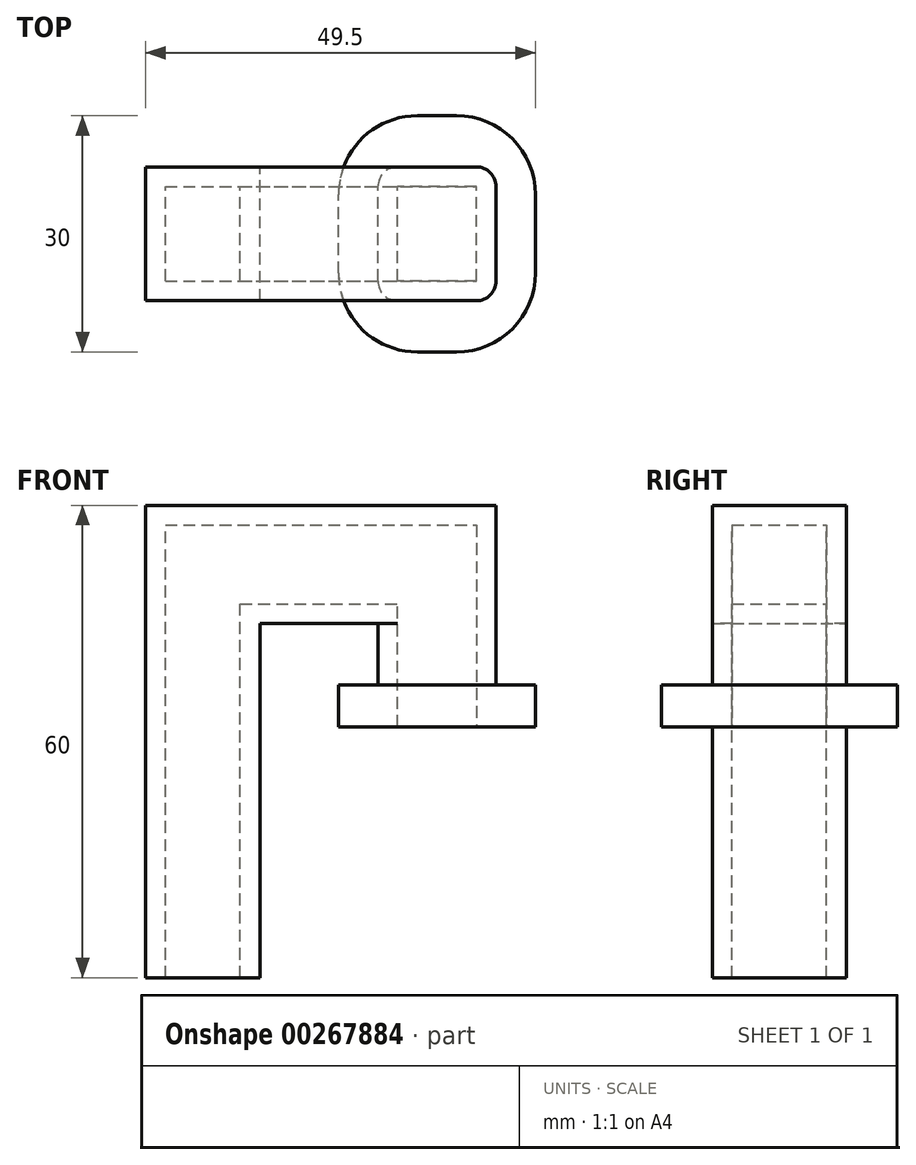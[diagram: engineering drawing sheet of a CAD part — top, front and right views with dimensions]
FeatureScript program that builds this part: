
annotation { "Feature Type Name" : "Feature", "Feature Type Description" : "" }
export const myFeature = defineFeature(function(context is Context, id is Id, definition is map)
    precondition{}
    {
        {
            var Q0;
            Q0=qCreatedBy(makeId("Front.planeOp"),FACE);
            var sketch = newSketch(context, id + "F0", { "sketchPlane" : qUnion([Q0])});
            skLineSegment(sketch, "E0", {"start": v(-4.8, -0.41) * mm, "end": v(-4.8, 59.59) * mm});
            skLineSegment(sketch, "E1", {"start": v(-4.8, -0.41) * mm, "end": v(9.7, -0.41) * mm});
            skLineSegment(sketch, "E2", {"start": v(9.7, -0.41) * mm, "end": v(9.7, 44.59) * mm});
            skLineSegment(sketch, "E3", {"start": v(9.7, 44.59) * mm, "end": v(24.7, 44.59) * mm});
            skLineSegment(sketch, "E4", {"start": v(39.7, 59.59) * mm, "end": v(39.7, 36.77) * mm});
            skLineSegment(sketch, "E5", {"start": v(39.7, 36.77) * mm, "end": v(24.7, 36.77) * mm});
            skLineSegment(sketch, "E6", {"start": v(24.7, 36.77) * mm, "end": v(24.7, 44.59) * mm});
            skLineSegment(sketch, "E7", {"start": v(24.7, 36.77) * mm, "end": v(19.7, 36.77) * mm});
            skLineSegment(sketch, "E8", {"start": v(19.7, 36.77) * mm, "end": v(19.7, 31.46) * mm});
            skLineSegment(sketch, "E9", {"start": v(19.7, 31.46) * mm, "end": v(44.7, 31.46) * mm});
            skLineSegment(sketch, "E10", {"start": v(44.7, 31.46) * mm, "end": v(44.7, 36.77) * mm});
            skLineSegment(sketch, "E11", {"start": v(44.7, 36.77) * mm, "end": v(39.7, 36.77) * mm});
            skLineSegment(sketch, "E12", {"start": v(-4.8, 59.59) * mm, "end": v(39.7, 59.59) * mm});
            skSolve(sketch);
        }
        {
            var Q0;
            Q0=makeQuery(id+"F0.imprint","IMPRINT",FACE,{"disambiguationData":[TD([[makeQuery(id+"F0.imprint","IMPRINT",EDGE,{"derivedFrom":sQuery(id+"F0.wireOp",EDGE,"E0")}),-1.0]])]});
            extrude(context, id + "F1", {"entities" : qUnion([Q0]), "endBound" : BoundingType.SYMMETRIC, "depth" : 17 * mm});
        }
        {
            var Q0;
            Q0=makeQuery(id+"F1.opExtrude","SWEPT_FACE",FACE,{"disambiguationData":[OSD([sQuery(id+"F0.wireOp",EDGE,"E1")])]});
            shell(context, id + "F2", {"entities" : qUnion([Q0]), "thickness" : 2.5 * mm});
        }
        {
            var Q0;
            Q0=makeQuery(id+"F0.imprint","IMPRINT",FACE,{"disambiguationData":[TD([[makeQuery(id+"F0.imprint","IMPRINT",EDGE,{"derivedFrom":sQuery(id+"F0.wireOp",EDGE,"E5")}),1.0]])]});
            extrude(context, id + "F3", {"entities" : qUnion([Q0]), "operationType" : NewBodyOperationType.ADD, "endBound" : BoundingType.SYMMETRIC, "depth" : 30 * mm});
        }
        {
            var Q0;
            Q0=makeQuery(id+"F3.opExtrude","SWEPT_FACE",FACE,{"disambiguationData":[OSD([sQuery(id+"F0.wireOp",EDGE,"E9")])]});
            var sketch = newSketch(context, id + "F4", { "sketchPlane" : qUnion([Q0])});
            skPoint(sketch, "E13.0", {"position": v(32.2, 15) * mm});
            skPoint(sketch, "E14.0", {"position": v(44.7, 0) * mm});
            skPoint(sketch, "E15.middle", {"position": v(32.2, 0) * mm});
            skLineSegment(sketch, "E16.0.0", {"start": v(44.7, -15) * mm, "end": v(19.7, -15) * mm});
            skLineSegment(sketch, "E16.0.1", {"start": v(19.7, -15) * mm, "end": v(19.7, 15) * mm});
            skLineSegment(sketch, "E16.0.2", {"start": v(19.7, 15) * mm, "end": v(44.7, 15) * mm});
            skLineSegment(sketch, "E16.0.3", {"start": v(44.7, 15) * mm, "end": v(44.7, -15) * mm});
            skLineSegment(sketch, "E17.0", {"start": v(39.7, 8.5) * mm, "end": v(39.7, -8.5) * mm});
            skLineSegment(sketch, "E18.0", {"start": v(39.7, 8.5) * mm, "end": v(24.7, 8.5) * mm});
            skLineSegment(sketch, "E19.0", {"start": v(24.7, 8.5) * mm, "end": v(24.7, -8.5) * mm});
            skLineSegment(sketch, "E20.0", {"start": v(39.7, -8.5) * mm, "end": v(24.7, -8.5) * mm});
            skLineSegment(sketch, "E21.0", {"start": v(37.2, 6) * mm, "end": v(37.2, -6) * mm});
            skLineSegment(sketch, "E22.0", {"start": v(37.2, -6) * mm, "end": v(27.2, -6) * mm});
            skLineSegment(sketch, "E23.0", {"start": v(37.2, 6) * mm, "end": v(27.2, 6) * mm});
            skLineSegment(sketch, "E24.0", {"start": v(27.2, 6) * mm, "end": v(27.2, -6) * mm});
            skSolve(sketch);
        }
        {
            var Q0;
            Q0=makeQuery(id+"F4.imprint","IMPRINT",FACE,{"disambiguationData":[TD([[makeQuery(id+"F4.imprint","IMPRINT",EDGE,{"derivedFrom":sQuery(id+"F4.wireOp",EDGE,"E21.0")}),-1.0]])]});
            var Q1;
            Q1=makeQuery(id+"F3.opExtrude","SWEPT_FACE",FACE,{"disambiguationData":[OSD([sQuery(id+"F0.wireOp",EDGE,"E5"),sQuery(id+"F0.wireOp",EDGE,"E7"),sQuery(id+"F0.wireOp",EDGE,"E11")])]});
            extrude(context, id + "F5", {"entities" : qUnion([Q0]), "operationType" : NewBodyOperationType.REMOVE, "oppositeDirection" : true, "endBoundEntityFace" : qUnion([Q1]), "depth" : 10 * mm});
        }
        {
            var Q0;
            Q0=makeQuery(id+"F3.opExtrude","CAP_EDGE",EDGE,{"disambiguationData":[OSD([sQuery(id+"F0.wireOp",EDGE,"E10")])],"isStart":false});
            var Q1;
            Q1=makeQuery(id+"F3.opExtrude","CAP_EDGE",EDGE,{"disambiguationData":[OSD([sQuery(id+"F0.wireOp",EDGE,"E8")])],"isStart":false});
            var Q2;
            Q2=makeQuery(id+"F3.opExtrude","CAP_EDGE",EDGE,{"disambiguationData":[OSD([sQuery(id+"F0.wireOp",EDGE,"E10")])],"isStart":true});
            var Q3;
            Q3=makeQuery(id+"F3.opExtrude","CAP_EDGE",EDGE,{"disambiguationData":[OSD([sQuery(id+"F0.wireOp",EDGE,"E8")])],"isStart":true});
            fillet(context, id + "F6", {"entities" : qUnion([Q0, Q1, Q2, Q3]), "radius" : 10 * mm, "tangentPropagation" : true, "allowEdgeOverflow" : false});
        }
        {
            var Q0;
            Q0=makeQuery(id+"F1.opExtrude","CAP_EDGE",EDGE,{"disambiguationData":[OSD([sQuery(id+"F0.wireOp",EDGE,"E4")])],"isStart":true});
            var Q1;
            Q1=makeQuery(id+"F1.opExtrude","CAP_EDGE",EDGE,{"disambiguationData":[OSD([sQuery(id+"F0.wireOp",EDGE,"E4")])],"isStart":false});
            var Q2;
            Q2=makeQuery(id+"F1.opExtrude","CAP_EDGE",EDGE,{"disambiguationData":[OSD([sQuery(id+"F0.wireOp",EDGE,"E6")])],"isStart":false});
            var Q3;
            Q3=makeQuery(id+"F1.opExtrude","CAP_EDGE",EDGE,{"disambiguationData":[OSD([sQuery(id+"F0.wireOp",EDGE,"E6")])],"isStart":true});
            fillet(context, id + "F7", {"entities" : qUnion([Q0, Q1, Q2, Q3]), "radius" : 2.5 * mm, "tangentPropagation" : true, "allowEdgeOverflow" : false});
        }
    });
